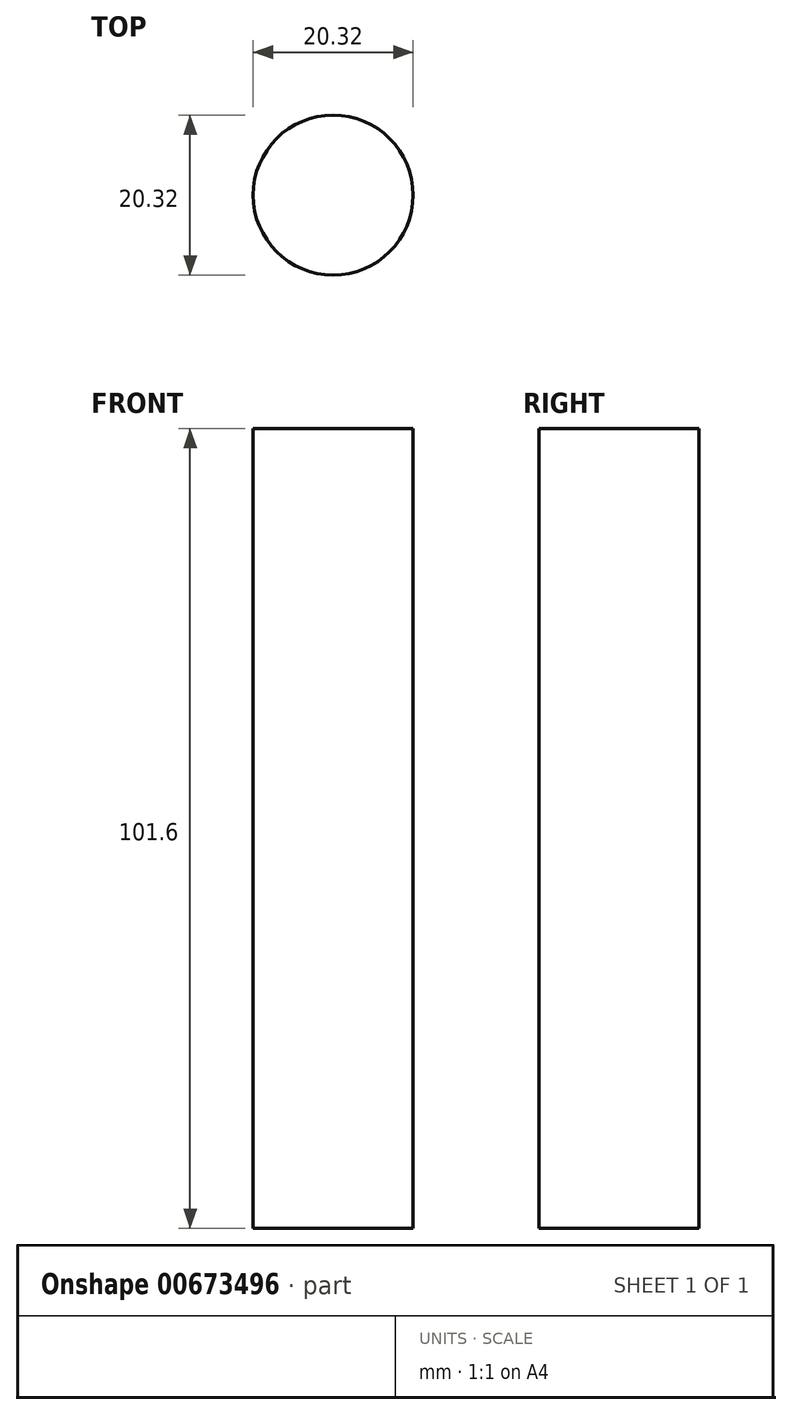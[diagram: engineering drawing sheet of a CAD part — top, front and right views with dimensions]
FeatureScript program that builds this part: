
annotation { "Feature Type Name" : "Feature", "Feature Type Description" : "" }
export const myFeature = defineFeature(function(context is Context, id is Id, definition is map)
    precondition{}
    {
        {
            var Q0;
            Q0=qCreatedBy(makeId("Top.planeOp"),FACE);
            var sketch = newSketch(context, id + "F0", { "sketchPlane" : qUnion([Q0])});
            skCircle(sketch, "E0", {"center": v(0, 0) * mm, "radius": 10.16 * mm});
            skSolve(sketch);
        }
        {
            var Q0;
            Q0=makeQuery(id+"F0.imprint","IMPRINT",FACE,{"disambiguationData":[TD([[makeQuery(id+"F0.imprint","IMPRINT",EDGE,{"derivedFrom":sQuery(id+"F0.wireOp",EDGE,"E0")}),1.0]])]});
            extrude(context, id + "F1", {"entities" : qUnion([Q0]), "depth" : 101.6 * mm, "offsetDistance" : 25.4 * mm});
        }
    });
